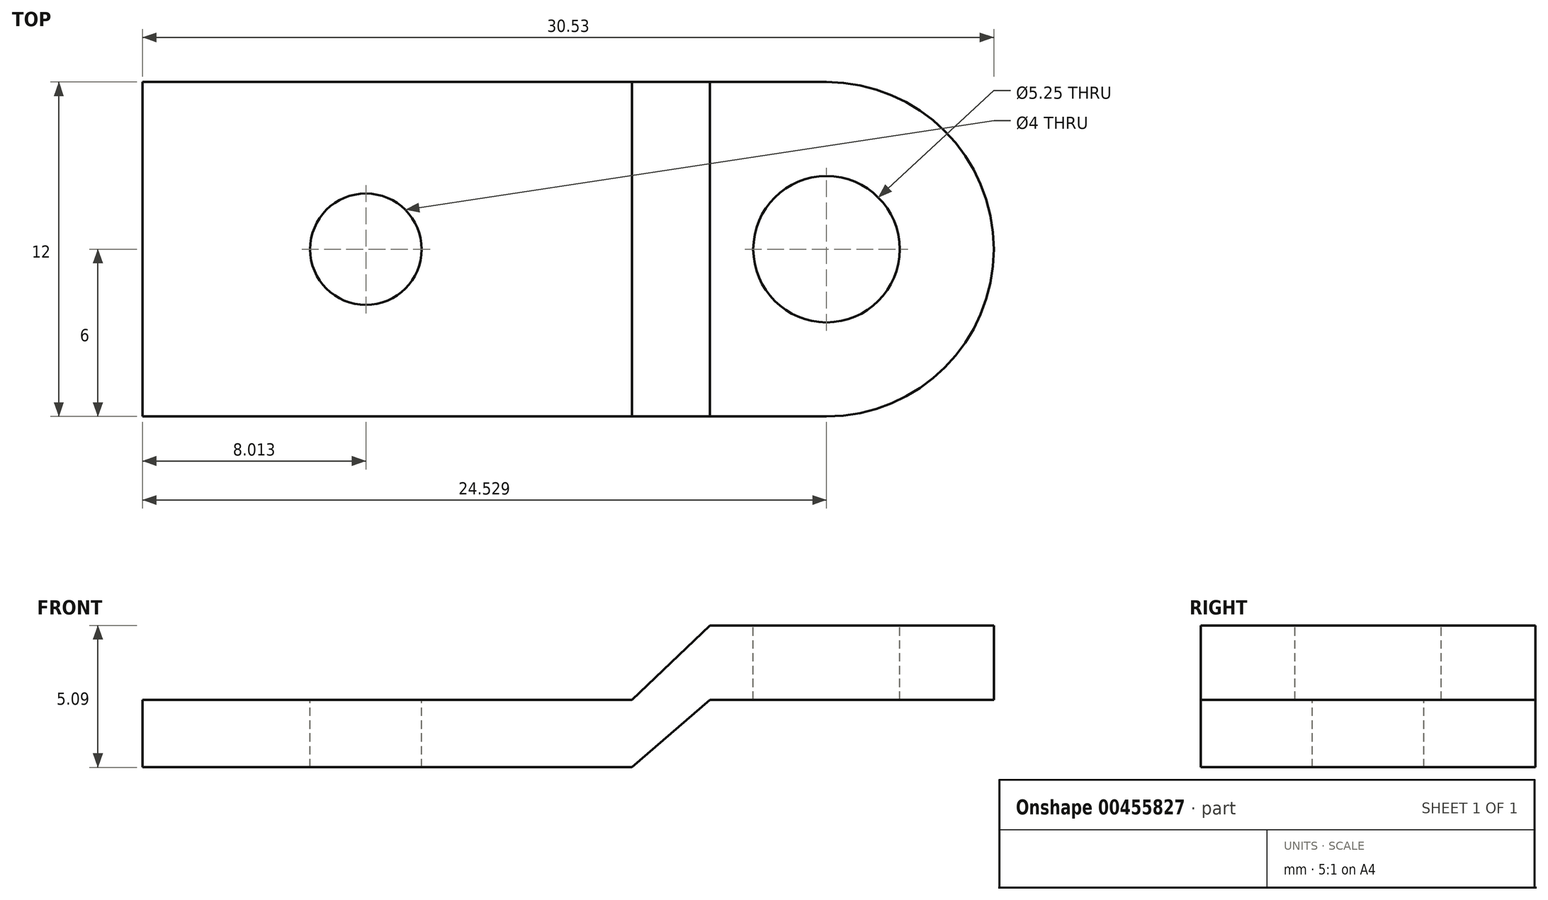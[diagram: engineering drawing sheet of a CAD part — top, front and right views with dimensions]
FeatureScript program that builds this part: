
annotation { "Feature Type Name" : "Feature", "Feature Type Description" : "" }
export const myFeature = defineFeature(function(context is Context, id is Id, definition is map)
    precondition{}
    {
        {
            var Q0;
            Q0=qCreatedBy(makeId("Front.planeOp"),FACE);
            var sketch = newSketch(context, id + "F0", { "sketchPlane" : qUnion([Q0])});
            skLineSegment(sketch, "E0", {"start": v(0, 0) * mm, "end": v(17.55, 0) * mm});
            skLineSegment(sketch, "E1", {"start": v(0, 0) * mm, "end": v(0, -2.42) * mm});
            skLineSegment(sketch, "E2", {"start": v(0, -2.42) * mm, "end": v(17.55, -2.42) * mm});
            skLineSegment(sketch, "E3", {"start": v(17.55, 0) * mm, "end": v(20.35, 2.67) * mm});
            skLineSegment(sketch, "E4", {"start": v(17.55, -2.42) * mm, "end": v(20.35, 0) * mm});
            skLineSegment(sketch, "E5", {"start": v(20.35, 2.67) * mm, "end": v(30.53, 2.67) * mm});
            skLineSegment(sketch, "E6", {"start": v(30.53, 2.67) * mm, "end": v(30.53, 0) * mm});
            skLineSegment(sketch, "E7", {"start": v(30.53, 0) * mm, "end": v(20.35, 0) * mm});
            skSolve(sketch);
        }
        {
            var Q0;
            Q0 = qSketchRegion(id + "F0", true);
            extrude(context, id + "F1", {"entities" : qUnion([Q0]), "depth" : 12 * mm});
        }
        {
            var Q0;
            Q0=makeQuery(id+"F1.opExtrude","CAP_EDGE",EDGE,{"disambiguationData":[OSD([sQuery(id+"F0.wireOp",EDGE,"E6")])],"isStart":true});
            fillet(context, id + "F2", {"entities" : qUnion([Q0]), "radius" : 6 * mm, "tangentPropagation" : true, "allowEdgeOverflow" : false});
        }
        {
            var Q0;
            Q0=makeQuery(id+"F1.opExtrude","CAP_EDGE",EDGE,{"disambiguationData":[OSD([sQuery(id+"F0.wireOp",EDGE,"E6")])],"isStart":false});
            fillet(context, id + "F3", {"entities" : qUnion([Q0]), "radius" : 6 * mm, "tangentPropagation" : true, "allowEdgeOverflow" : false});
        }
        {
            var Q0;
            Q0=makeQuery(id+"F1.opExtrude","SWEPT_FACE",FACE,{"disambiguationData":[OSD([sQuery(id+"F0.wireOp",EDGE,"E5")])]});
            var sketch = newSketch(context, id + "F4", { "sketchPlane" : qUnion([Q0])});
            skCircle(sketch, "E8", {"center": v(24.53, -6) * mm, "radius": 2.58 * mm});
            skSolve(sketch);
        }
        {
            var Q0;
            Q0=sQuery(id+"F4.wireOp",VERTEX,"E8.center");
            var Q1;
            Q1=makeQuery(id+"F1.opExtrude","SWEPT_BODY",BODY,{"disambiguationData":[OSD([sQuery(id+"F0.wireOp",EDGE,"E0"),sQuery(id+"F0.wireOp",EDGE,"E1"),sQuery(id+"F0.wireOp",EDGE,"E2"),sQuery(id+"F0.wireOp",EDGE,"E3"),sQuery(id+"F0.wireOp",EDGE,"E4"),sQuery(id+"F0.wireOp",EDGE,"E5"),sQuery(id+"F0.wireOp",EDGE,"E6"),sQuery(id+"F0.wireOp",EDGE,"E7")])]});
            hole(context, id + "F5", {"style" : HoleStyle.SIMPLE, "endStyle" : HoleEndStyle.BLIND, "holeDiameter" : 5.25 * mm, "holeDepth" : 12 * mm, "isTappedThrough" : true, "tappedDepth" : 12 * mm, "tapClearance" : 3, "locations" : qUnion([Q0]), "scope" : qUnion([Q1])});
        }
        {
            var Q0;
            Q0=makeQuery(id+"F1.opExtrude","SWEPT_FACE",FACE,{"disambiguationData":[OSD([sQuery(id+"F0.wireOp",EDGE,"E0")])]});
            var sketch = newSketch(context, id + "F6", { "sketchPlane" : qUnion([Q0])});
            skLineSegment(sketch, "E9", {"start": v(0, -6) * mm, "end": v(8.01, -6) * mm});
            skSolve(sketch);
        }
        {
            var Q0;
            Q0=sQuery(id+"F6.wireOp",VERTEX,"E9.end");
            var Q1;
            Q1=makeQuery(id+"F1.opExtrude","SWEPT_BODY",BODY,{"disambiguationData":[OSD([sQuery(id+"F0.wireOp",EDGE,"E0"),sQuery(id+"F0.wireOp",EDGE,"E1"),sQuery(id+"F0.wireOp",EDGE,"E2"),sQuery(id+"F0.wireOp",EDGE,"E3"),sQuery(id+"F0.wireOp",EDGE,"E4"),sQuery(id+"F0.wireOp",EDGE,"E5"),sQuery(id+"F0.wireOp",EDGE,"E6"),sQuery(id+"F0.wireOp",EDGE,"E7")])]});
            hole(context, id + "F7", {"style" : HoleStyle.SIMPLE, "endStyle" : HoleEndStyle.BLIND, "holeDiameter" : 4 * mm, "holeDepth" : 12 * mm, "isTappedThrough" : true, "tappedDepth" : 12 * mm, "tapClearance" : 3, "locations" : qUnion([Q0]), "scope" : qUnion([Q1])});
        }
    });
